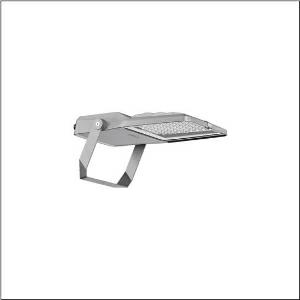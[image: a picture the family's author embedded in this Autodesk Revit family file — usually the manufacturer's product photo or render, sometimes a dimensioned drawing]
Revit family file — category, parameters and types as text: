
# Revit family: floodlight_fl_21_mini___pl61_5xa7772c3c1a_e4fd
name_source: partatom
category: Lighting Fixtures
units: mm (PartAtom-declared; Revit-internal decimal feet)

## family parameters
Cut with Voids When Loaded = No
Host = Face
Light Source = No
Part Type = Normal
Room Calculation Point = No
Round Connector Dimension = Use Diameter
Shared = No

## types (1)
- --- (1 x LED, 10320 lm, 87.2 W, 3000K)
    Apparent Load = 87 VA
    CIE Flux Codes = 33 65 98 100 100
    Color Rendering = 80
    Color Temperature = 3000K
    Default Elevation = 1800 mm
    Description = Floodlight FL 21 mini, floodlight, primary light control with lens, of PMMA, primary optical cover: protective disc, of toughened safety glass, transparent, light distribution: PL61, light emission: direct distribution, installation type: surface-mounted, LED, High Power LED, rated luminous flux: 10.320lm, luminous efficacy: 118lm/W, light colour: 830, colour temperature: 3000K, control gear: ECG iQ, control: Street-Remote, Auto-Match, Temp-Guard, Night-Set, Smart-Wire, Desk-Remote (wireless, voltage-free reading and setting of iQ features in the workshop via application-optimized NFC function/RFID function), optimised constant luminous flux control (CLO 2.0), with terminal, 6-pole, mains connection: 220..240V, AC, 50/60Hz, start of lifetime: 87W, end of lifetime: 92W, reduction: 40W, luminaire housing, of diecast aluminium, powder-coated, Siteco® metallic grey (DB 702S), corrosivity category C5 according to DIN EN ISO 12944, mounting bracket, of steel, galvanised, powder-coated, Siteco® metallic grey (DB 702S), protection rating (complete): IP66, insulation class (complete): insulation class II (safety insulation), certification: CE, ENEC, VDE, protection symbol: D, impact resistance: IK08, permissible operating ambient temperature: -40..+40°C, permissible operating ambient temperature for outdoor applications: -40..+50°C, standard: DIN EN 12944, packaging unit: 1 piece

Light Distribution: PL61
    Height = 70 mm
    Lamp = 1 x LED
    Lamp Light Flux = 10320 lm
    Lamp Power = 87.2 W
    Lamp count = 1
    Length = 485 mm
    Luminous efficacy = 118 lm/W
    Manufacturer = Siteco
    ModVariant = No
    Model = 5XA7772C3C1A
    Number of Poles = 1
    OnlyDefault = Yes
    Power Factor = 1
    Product Name = Floodlight FL 21 mini | PL61
    Product group = floodlight | pylon top
    ProductGroupID = 6101
    Protection Class = Protection class II
    Protection Degree = IP 66
    RLX_Detail_Level = 1
    RlxData = <blob elided: 96177 chars, md5=376c9bde>
    Socket = socket
    Standby Power = 0 W
    System Light Flux = 10320 lm
    System Power = 87 W
    Type Comments = factory setting: luminous flux: 100 % | dim-lin: 254 | 456 mA
    Type Image = l_1006845.jpg
    URL = http://relux.com
    VarID = @adj_085333
    Voltage = 0 V
    Weight = 0.00 kg
    Width = 337 mm

## geometry (parser evidence)
native form markers: Blend x4, Sweep x13
no freeform markers — native parametric forms only
